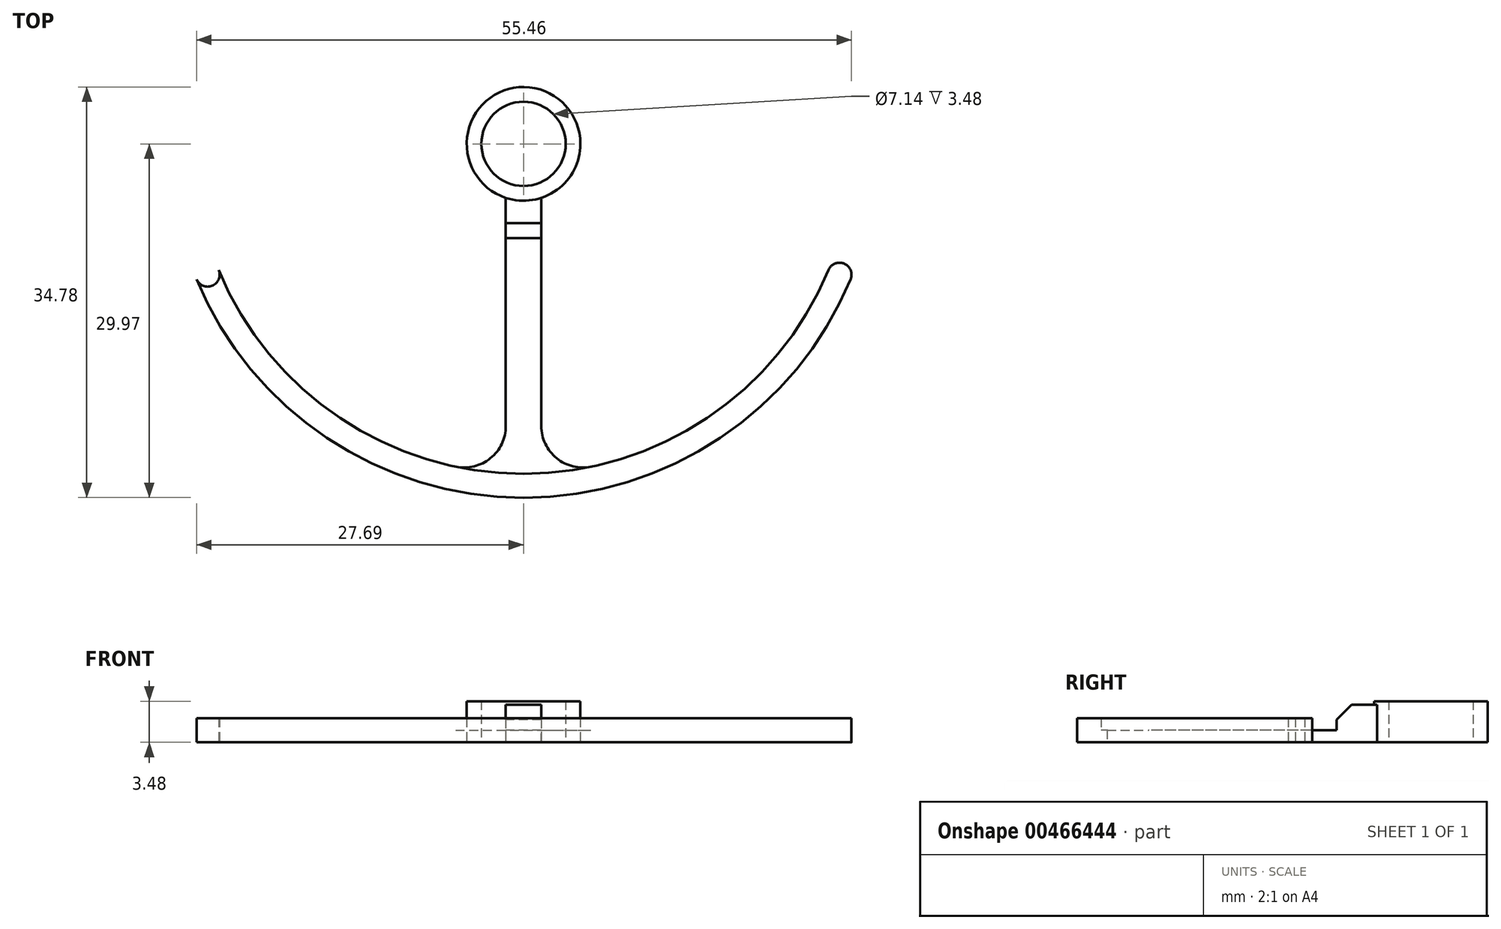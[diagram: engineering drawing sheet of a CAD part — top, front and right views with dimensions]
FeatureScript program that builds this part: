
annotation { "Feature Type Name" : "Feature", "Feature Type Description" : "" }
export const myFeature = defineFeature(function(context is Context, id is Id, definition is map)
    precondition{}
    {
        {
            var Q0;
            Q0=qCreatedBy(makeId("Top.planeOp"),FACE);
            var sketch = newSketch(context, id + "F0", { "sketchPlane" : qUnion([Q0])});
            skCircle(sketch, "E0", {"center": v(0, 0) * mm, "radius": 28.96 * mm, "construction": true});
            skCircle(sketch, "E1", {"center": v(0, 0) * mm, "radius": 3.57 * mm});
            skCircle(sketch, "E2", {"center": v(0, 0) * mm, "radius": 4.81 * mm});
            skSolve(sketch);
        }
        {
            var Q0;
            Q0=makeQuery(id+"F0.imprint","IMPRINT",FACE,{"disambiguationData":[TD([[makeQuery(id+"F0.imprint","IMPRINT",EDGE,{"derivedFrom":sQuery(id+"F0.wireOp",EDGE,"E1")}),-1.0]])]});
            extrude(context, id + "F1", {"entities" : qUnion([Q0]), "depth" : 3.48 * mm, "offsetDistance" : 25.4 * mm});
        }
        {
            var Q0;
            Q0=qCreatedBy(makeId("Top.planeOp"),FACE);
            var sketch = newSketch(context, id + "F2", { "sketchPlane" : qUnion([Q0])});
            skLineSegment(sketch, "E3.bottom", {"start": v(-1.5, -4.57) * mm, "end": v(1.5, -4.57) * mm});
            skLineSegment(sketch, "E3.top", {"start": v(-1.5, -28.92) * mm, "end": v(1.5, -28.92) * mm});
            skLineSegment(sketch, "E3.left", {"start": v(-1.5, -4.57) * mm, "end": v(-1.5, -28.92) * mm});
            skLineSegment(sketch, "E3.right", {"start": v(1.5, -4.57) * mm, "end": v(1.5, -28.92) * mm});
            skSolve(sketch);
        }
        {
            var Q0;
            Q0=makeQuery(id+"F2.imprint","IMPRINT",FACE,{"disambiguationData":[TD([[makeQuery(id+"F2.imprint","IMPRINT",EDGE,{"derivedFrom":sQuery(id+"F2.wireOp",EDGE,"E3.bottom")}),-1.0]])]});
            extrude(context, id + "F3", {"entities" : qUnion([Q0]), "operationType" : NewBodyOperationType.ADD, "depth" : 1.02 * mm, "offsetDistance" : 25.4 * mm});
        }
        {
            var Q0;
            Q0=qCreatedBy(makeId("Top.planeOp"),FACE);
            var sketch = newSketch(context, id + "F4", { "sketchPlane" : qUnion([Q0])});
            skLineSegment(sketch, "E4", {"start": v(0, 0) * mm, "end": v(46.93, -19.44) * mm, "construction": true});
            skLineSegment(sketch, "E5", {"start": v(0, 0) * mm, "end": v(-46.93, -19.44) * mm, "construction": true});
            skCircle(sketch, "E6", {"center": v(26.75, -11.08) * mm, "radius": 1.02 * mm});
            skCircle(sketch, "E7.MirrorC", {"center": v(-26.75, -11.08) * mm, "radius": 1.02 * mm});
            skArc(sketch, "E8", {"start": v(-25.81, -10.7) * mm, "mid": v(0, -27.94) * mm, "end": v(25.81, -10.7) * mm});
            skArc(sketch, "E9", {"start": v(-27.7, -11.47) * mm, "mid": v(0, -29.97) * mm, "end": v(27.7, -11.47) * mm});
            skSolve(sketch);
        }
        {
            var Q0;
            {var subQ0=sQuery(id+"F4.wireOp",EDGE,"E8");Q0=makeQuery(id+"F4.imprint","IMPRINT",FACE,{"disambiguationData":[TD([[makeQuery(id+"F4.imprint","IMPRINT",EDGE,{"derivedFrom":subQ0}),-1.0]])]});}
            var Q1;
            {var subQ0=sQuery(id+"F4.wireOp",EDGE,"E6");var subQ1=makeQuery(id+"F4.imprint","INTERSECT",VERTEX,{"derivedFrom":[subQ0,sQuery(id+"F4.wireOp",EDGE,"E8")]});Q1=makeQuery(id+"F4.imprint","IMPRINT",FACE,{"disambiguationData":[TD([[makeQuery(id+"F4.imprint","IMPRINT",EDGE,{"disambiguationData":[TD([[subQ1,-1.0]])],"derivedFrom":subQ0}),1.0]])]});}
            var Q2;
            {var subQ0=sQuery(id+"F4.wireOp",EDGE,"E7.MirrorC");var subQ1=makeQuery(id+"F4.imprint","INTERSECT",VERTEX,{"derivedFrom":[subQ0,sQuery(id+"F4.wireOp",EDGE,"E8")]});Q2=makeQuery(id+"F4.imprint","IMPRINT",FACE,{"disambiguationData":[TD([[makeQuery(id+"F4.imprint","IMPRINT",EDGE,{"disambiguationData":[TD([[subQ1,-1.0]])],"derivedFrom":subQ0}),-1.0]])]});}
            extrude(context, id + "F5", {"entities" : qUnion([Q0, Q1, Q2]), "operationType" : NewBodyOperationType.ADD, "depth" : 2.03 * mm, "offsetDistance" : 25.4 * mm});
        }
        {
            var Q0;
            Q0=makeQuery(id+"F5.boolean.opBoolean","INTERSECT",EDGE,{"derivedFrom":[makeQuery(id+"F3.opExtrude","SWEPT_FACE",FACE,{"disambiguationData":[OSD([sQuery(id+"F2.wireOp",EDGE,"E3.right")])]}),makeQuery(id+"F5.opExtrude","SWEPT_FACE",FACE,{"disambiguationData":[OSD([sQuery(id+"F4.wireOp",EDGE,"E8")])]})]});
            var Q1;
            Q1=makeQuery(id+"F5.boolean.opBoolean","INTERSECT",EDGE,{"derivedFrom":[makeQuery(id+"F3.opExtrude","SWEPT_FACE",FACE,{"disambiguationData":[OSD([sQuery(id+"F2.wireOp",EDGE,"E3.left")])]}),makeQuery(id+"F5.opExtrude","SWEPT_FACE",FACE,{"disambiguationData":[OSD([sQuery(id+"F4.wireOp",EDGE,"E8")])]})]});
            fillet(context, id + "F6", {"entities" : qUnion([Q0, Q1]), "radius" : 3.52 * mm, "tangentPropagation" : true, "allowEdgeOverflow" : false});
        }
        {
            var Q0;
            Q0=qCreatedBy(makeId("Top.planeOp"),FACE);
            var sketch = newSketch(context, id + "F7", { "sketchPlane" : qUnion([Q0])});
            skLineSegment(sketch, "E10.bottom", {"start": v(-1.5, -4.57) * mm, "end": v(1.5, -4.57) * mm});
            skLineSegment(sketch, "E10.top", {"start": v(-1.5, -7.99) * mm, "end": v(1.5, -7.99) * mm});
            skLineSegment(sketch, "E10.left", {"start": v(-1.5, -4.57) * mm, "end": v(-1.5, -7.99) * mm});
            skLineSegment(sketch, "E10.right", {"start": v(1.5, -4.57) * mm, "end": v(1.5, -7.99) * mm});
            skSolve(sketch);
        }
        {
            var Q0;
            Q0 = qSketchRegion(id + "F7", true);
            extrude(context, id + "F8", {"entities" : qUnion([Q0]), "operationType" : NewBodyOperationType.ADD, "depth" : 3.2 * mm, "offsetDistance" : 25.4 * mm});
        }
        {
            var Q0;
            Q0=makeQuery(id+"F8.opExtrude","CAP_EDGE",EDGE,{"disambiguationData":[OSD([sQuery(id+"F7.wireOp",EDGE,"E10.top")])],"isStart":false});
            chamfer(context, id + "F9", {"entities" : qUnion([Q0]), "width" : 1.27 * mm, "tangentPropagation" : true});
        }
    });
